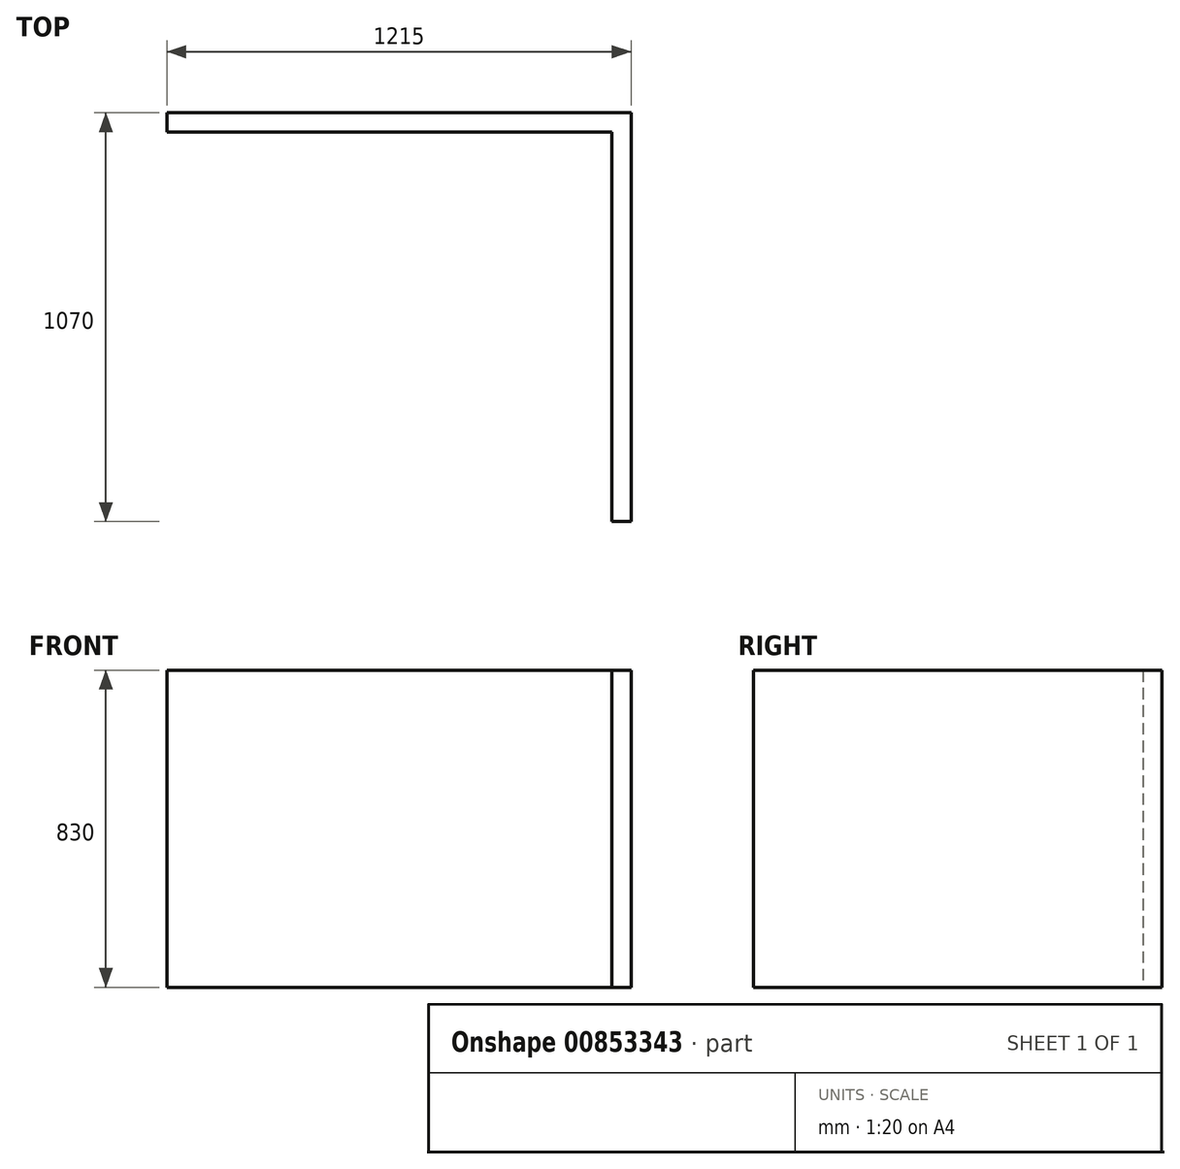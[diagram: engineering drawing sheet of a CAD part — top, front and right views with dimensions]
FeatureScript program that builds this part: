
annotation { "Feature Type Name" : "Feature", "Feature Type Description" : "" }
export const myFeature = defineFeature(function(context is Context, id is Id, definition is map)
    precondition{}
    {
        {
            var Q0;
            Q0=qCreatedBy(makeId("Top.planeOp"),FACE);
            var sketch = newSketch(context, id + "F0", { "sketchPlane" : qUnion([Q0])});
            skLineSegment(sketch, "E0", {"start": v(-924.97, 225.68) * mm, "end": v(290.03, 225.68) * mm});
            skLineSegment(sketch, "E1", {"start": v(290.03, 225.68) * mm, "end": v(290.03, -844.32) * mm});
            skLineSegment(sketch, "E2", {"start": v(-924.97, 225.68) * mm, "end": v(-924.97, 175.68) * mm});
            skLineSegment(sketch, "E3", {"start": v(-924.97, 175.68) * mm, "end": v(240.03, 175.68) * mm});
            skLineSegment(sketch, "E4", {"start": v(290.03, -844.32) * mm, "end": v(240.03, -844.32) * mm});
            skLineSegment(sketch, "E5", {"start": v(240.03, 175.68) * mm, "end": v(240.03, -844.32) * mm});
            skSolve(sketch);
        }
        {
            var Q0;
            Q0 = qSketchRegion(id + "F0", true);
            extrude(context, id + "F1", {"entities" : qUnion([Q0]), "depth" : 830 * mm, "offsetDistance" : 25 * mm});
        }
    });
